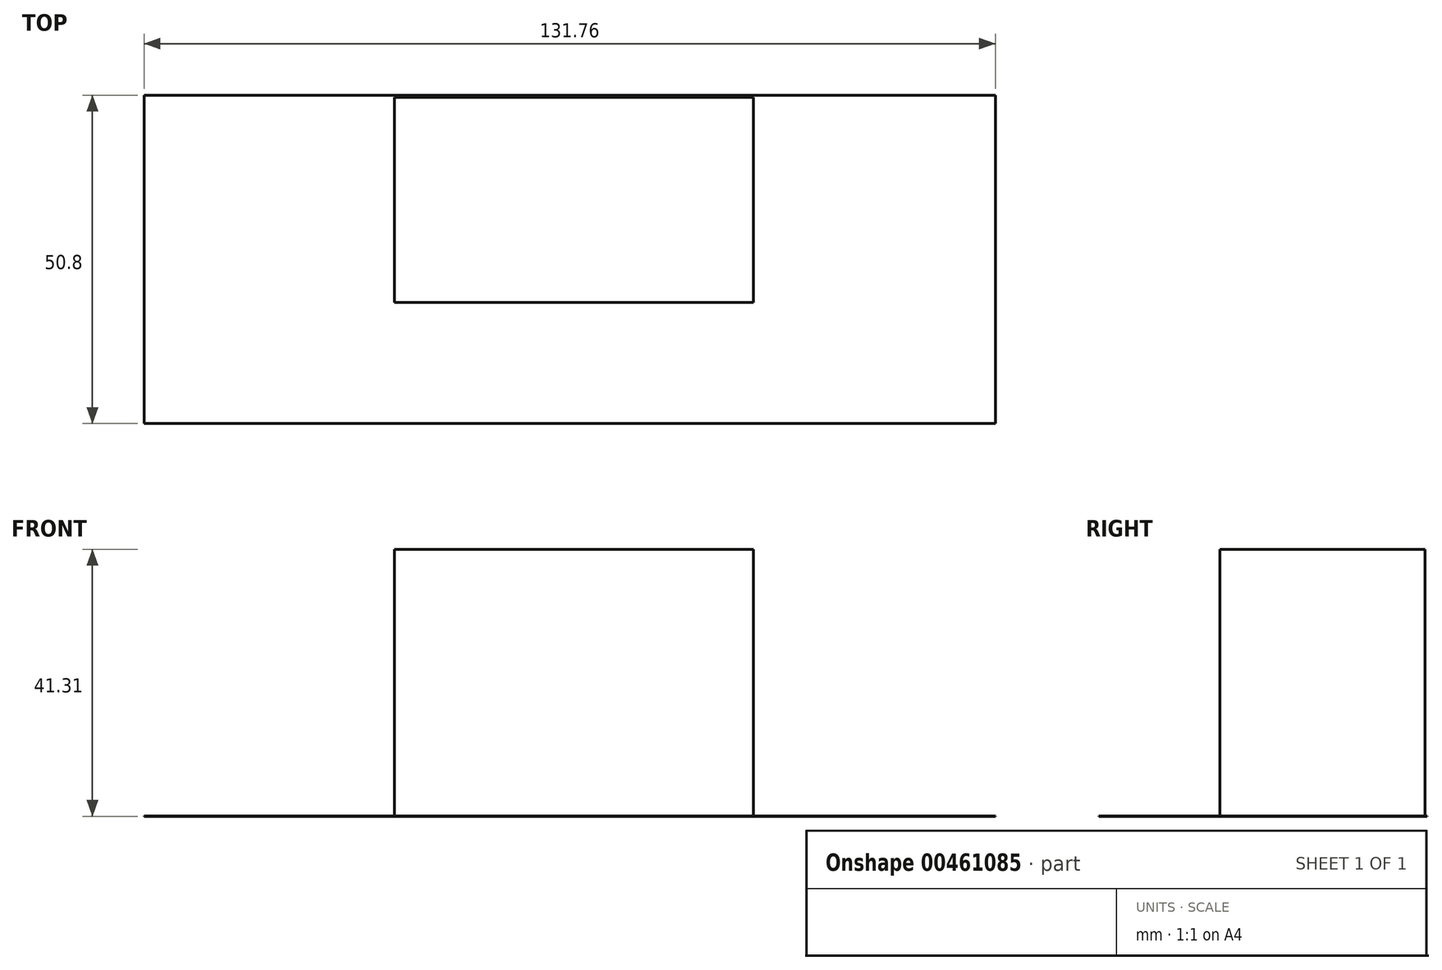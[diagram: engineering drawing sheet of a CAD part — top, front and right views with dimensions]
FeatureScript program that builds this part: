
annotation { "Feature Type Name" : "Feature", "Feature Type Description" : "" }
export const myFeature = defineFeature(function(context is Context, id is Id, definition is map)
    precondition{}
    {
        {
            var Q0;
            Q0=qCreatedBy(makeId("Top.planeOp"),FACE);
            var sketch = newSketch(context, id + "F0", { "sketchPlane" : qUnion([Q0])});
            skLineSegment(sketch, "E0.bottom", {"start": v(-102.27, 17.71) * mm, "end": v(29.5, 17.71) * mm});
            skLineSegment(sketch, "E0.top", {"start": v(-102.27, -33.09) * mm, "end": v(29.5, -33.09) * mm});
            skLineSegment(sketch, "E0.left", {"start": v(-102.27, 17.71) * mm, "end": v(-102.27, -33.09) * mm});
            skLineSegment(sketch, "E0.right", {"start": v(29.5, 17.71) * mm, "end": v(29.5, -33.09) * mm});
            skSolve(sketch);
        }
        {
            var Q0;
            Q0=makeQuery(id+"F0.imprint","IMPRINT",FACE,{"disambiguationData":[TD([[makeQuery(id+"F0.imprint","IMPRINT",EDGE,{"derivedFrom":sQuery(id+"F0.wireOp",EDGE,"E0.bottom")}),-1.0]])]});
            extrude(context, id + "F1", {"entities" : qUnion([Q0]), "depth" : 7 / 203.2 * mm});
        }
        {
            var Q0;
            Q0=makeQuery(id+"F1.opExtrude","CAP_FACE",FACE,{"disambiguationData":[OSD([sQuery(id+"F0.wireOp",EDGE,"E0.bottom"),sQuery(id+"F0.wireOp",EDGE,"E0.top"),sQuery(id+"F0.wireOp",EDGE,"E0.left"),sQuery(id+"F0.wireOp",EDGE,"E0.right")])],"isStart":false});
            var sketch = newSketch(context, id + "F2", { "sketchPlane" : qUnion([Q0])});
            skLineSegment(sketch, "E1", {"start": v(29.5, 17.71) * mm, "end": v(-8.6, 17.71) * mm});
            skSolve(sketch);
        }
        {
            var Q0;
            {var subQ2=sQuery(id+"F2.wireOp",EDGE,"E1");Q0=makeQuery(id+"F2.imprint","IMPRINT",FACE,{"disambiguationData":[TD([[makeQuery(id+"F2.imprint","IMPRINT",EDGE,{"derivedFrom":subQ2}),-1.0]])]});}
            var sketch = newSketch(context, id + "F3", { "sketchPlane" : qUnion([Q0])});
            skLineSegment(sketch, "E2.bottom", {"start": v(-7.96, 17.39) * mm, "end": v(-63.53, 17.39) * mm});
            skLineSegment(sketch, "E2.top", {"start": v(-7.96, -14.36) * mm, "end": v(-63.53, -14.36) * mm});
            skLineSegment(sketch, "E2.left", {"start": v(-7.96, 17.39) * mm, "end": v(-7.96, -14.36) * mm});
            skLineSegment(sketch, "E2.right", {"start": v(-63.53, 17.39) * mm, "end": v(-63.53, -14.36) * mm});
            skSolve(sketch);
        }
        {
            var Q0;
            Q0 = qSketchRegion(id + "F3", true);
            extrude(context, id + "F4", {"entities" : qUnion([Q0]), "operationType" : NewBodyOperationType.ADD, "depth" : 41.27 * mm});
        }
    });
